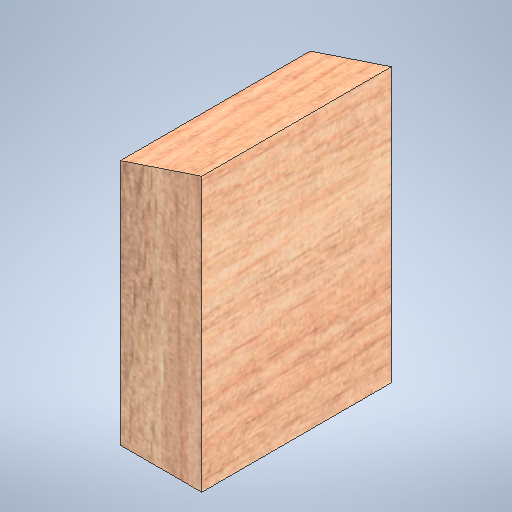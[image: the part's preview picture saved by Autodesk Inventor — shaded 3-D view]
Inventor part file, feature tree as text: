
AUTODESK INVENTOR PART (.ipt)
format: ipt  version: 2025.1 (Build 291241020, 241B)  size: 454,656 bytes
history: native  units: in
note: dims shown in document units (in); Inventor stores cm internally (conversion verified against a paired STEP export)
features: extrude x1, sketch x1
ambient origin geometry x8: Origin, YZ Plane, XZ Plane, XY Plane, X Axis, Y Axis, Z Axis, Center Point
bodies: Solid1 (feature_tree)
feature tree (2):
  extrude  "Extrusion1"  Depth=3.5in
  sketch  "Sketch1"  dims[d0=4.547in d1=5.047in d2=1.5in d3=3.5in d4=0.0in]
